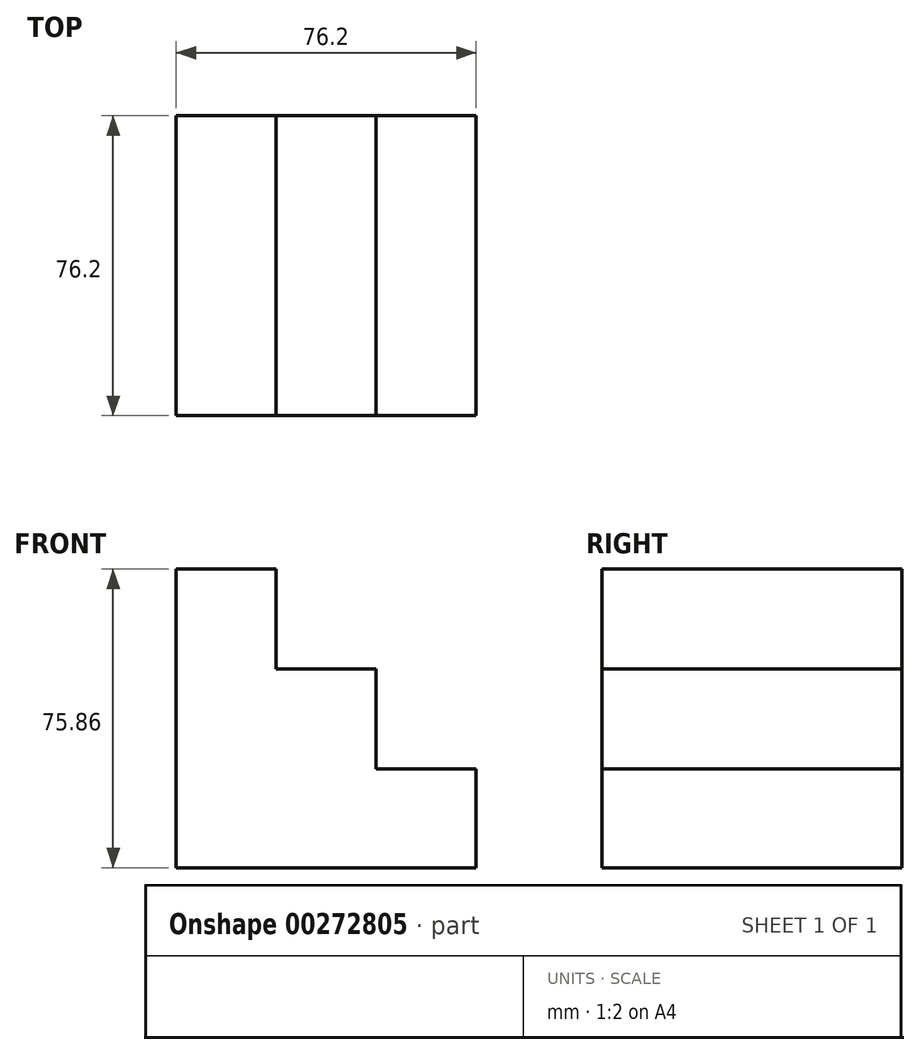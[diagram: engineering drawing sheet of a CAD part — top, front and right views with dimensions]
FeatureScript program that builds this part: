
annotation { "Feature Type Name" : "Feature", "Feature Type Description" : "" }
export const myFeature = defineFeature(function(context is Context, id is Id, definition is map)
    precondition{}
    {
        {
            var Q0;
            Q0=qCreatedBy(makeId("Front.planeOp"),FACE);
            var sketch = newSketch(context, id + "F0", { "sketchPlane" : qUnion([Q0])});
            skLineSegment(sketch, "E0", {"start": v(0, 0) * mm, "end": v(-76.2, 0) * mm});
            skLineSegment(sketch, "E1", {"start": v(-76.2, 0) * mm, "end": v(-76.2, 75.86) * mm});
            skLineSegment(sketch, "E2", {"start": v(-76.2, 75.86) * mm, "end": v(-50.8, 75.86) * mm});
            skLineSegment(sketch, "E3", {"start": v(-50.8, 75.86) * mm, "end": v(-50.8, 50.46) * mm});
            skLineSegment(sketch, "E4", {"start": v(-50.8, 50.46) * mm, "end": v(-25.4, 50.46) * mm});
            skLineSegment(sketch, "E5", {"start": v(-25.4, 50.46) * mm, "end": v(-25.4, 25.06) * mm});
            skLineSegment(sketch, "E6", {"start": v(-25.4, 25.06) * mm, "end": v(0, 25.06) * mm});
            skLineSegment(sketch, "E7", {"start": v(0, 25.06) * mm, "end": v(0, 0) * mm});
            skSolve(sketch);
        }
        {
            var Q0;
            Q0=makeQuery(id+"F0.imprint","IMPRINT",FACE,{"disambiguationData":[TD([[makeQuery(id+"F0.imprint","IMPRINT",EDGE,{"derivedFrom":sQuery(id+"F0.wireOp",EDGE,"E0")}),-1.0]])]});
            extrude(context, id + "F1", {"entities" : qUnion([Q0]), "depth" : 76.2 * mm});
        }
    });
